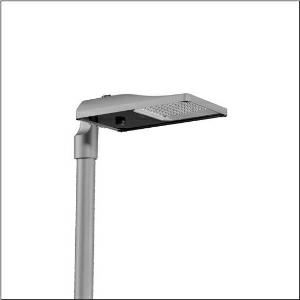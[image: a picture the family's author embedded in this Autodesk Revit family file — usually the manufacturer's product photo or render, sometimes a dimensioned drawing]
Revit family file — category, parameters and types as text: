
# Revit family: streetlight_sl_31_midi___st0_5a_5xh7b5at08qa_40ba
name_source: partatom
category: Lighting Fixtures
units: mm (PartAtom-declared; Revit-internal decimal feet)

## family parameters
Cut with Voids When Loaded = No
Host = Face
Light Source = No
Part Type = Normal
Room Calculation Point = No
Round Connector Dimension = Use Diameter
Shared = No

## types (1)
- --- (1 x LED, 21420 lm, 163.3 W, 3000K)
    Apparent Load = 163 VA
    CIE Flux Codes = 43 76 97 100 100
    Color Rendering = 80
    Color Temperature = 3000K
    Default Elevation = 1800 mm
    Description = Streetlight SL 31 midi D4i mast luminaire for post-top, side-entry; light control with lens of PMMA; light distribution: ST0.5a, direct asymmetric distribution, for standard-compliant lighting for roads and squares; LED: luminous flux: 21.420lm, light colour: 830, colour temperature: 3000K; luminous efficacy: 131,2lm/W; control: pre-setting: logarithmic dimming characteristic, flexible luminous flux parameterisation, time-dependent luminous flux control, constant luminous flux control, power reduction, intelligent temperature release in ECG and LED module, overheat protection; luminaire housing, of diecast aluminium, SITECO metallic grey (DB 702S), corrosivity category C5 high according to DIN EN ISO 12944; cover of toughened safety glass, transparent, opened without tools; mast flange of diecast aluminium, SITECO metallic grey (DB 702S), spigot size: 76/60mm, mast flange included unmounted; cable length: 14,5m, connection cable pre-assembled; mains connection: 220..240V, AC, 50/60Hz; power consumption (at start of service life): 163,3W / (at end of service life): 178,2W / (with reduced operation 50%): 72,4W; protection rating (complete): IP66; insulation class (complete): insulation class II (safety insulation); impact resistance: IK09; certification: CE, ENEC, ENEC+, VDE, UKCA, ZD4i; permissible operating ambient temperature for outdoor applications: -40..+50°C; packaging unit: 1 piece

Light Distribution: ST0.5a
    Height = 79 mm
    Lamp = 1 x LED
    Lamp Light Flux = 21420 lm
    Lamp Power = 163.3 W
    Lamp count = 1
    Length = 577 mm
    Luminous efficacy = 131 lm/W
    Manufacturer = Siteco
    ModVariant = No
    Model = 5XH7B5AT08QA
    Number of Poles = 1
    OnlyDefault = Yes
    Power Factor = 1
    Product Name = Streetlight SL 31 midi | ST0.5a
    Product group = mast luminaire | pylon top
    ProductGroupID = 6100
    Protection Class = Protection class II
    Protection Degree = IP 66
    RLX_Detail_Level = 1
    RLX_Emergency_Light_Flux = 0 lm
    RLX_Emergency_Type = 0
    RLX_Emergency_Type_DB = No
    RlxData = <blob elided: 54241 chars, md5=6adfd569>
    Socket = socket
    Standby Power = 0 W
    System Light Flux = 21420 lm
    System Power = 163 W
    Type Comments = factory setting: luminous flux: 100 % | dim-lin: 254 | 865 mA
    Type Image = l_1300321.jpg
    URL = http://relux.com
    VarID = @adj_064037
    Voltage = 0 V
    Weight = 0.00 kg
    Width = 362 mm

## geometry (parser evidence)
native form markers: Blend x4, Sweep x12
no freeform markers — native parametric forms only
